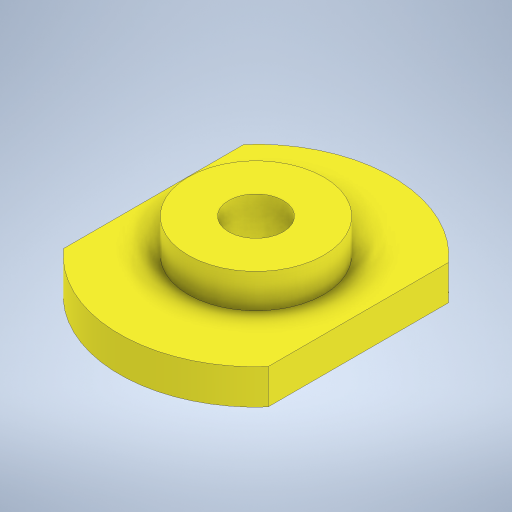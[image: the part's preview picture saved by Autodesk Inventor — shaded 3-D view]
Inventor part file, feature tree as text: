
AUTODESK INVENTOR PART (.ipt)
format: ipt  version: 2024 (Build 280153020, 153B)  size: 266,240 bytes
history: native  units: mm
features: extrude x4, sketch x3, mirror x1, projected_geometry x1
ambient origin geometry x8: Origin, YZ Plane, XZ Plane, XY Plane, X Axis, Y Axis, Z Axis, Center Point
bodies: Solid1 (feature_tree)
feature tree (9):
  sketch  "Sketch1"  dims[d0=7.95mm d1=3.2mm]
  extrude  "Extrusion1"  Depth=3.2mm
  extrude  "Extrusion2"  Depth=2.0mm TaperAngle=0.0deg
  extrude  "Extrusion4"  Depth=2.0mm
  mirror  "Mirror1"
  extrude  "Extrusion5"  Depth=2.0mm TaperAngle=0.0deg
  sketch  "Sketch3"  dims[d2=16.0mm d3=2.0mm d4=0.0mm]
  sketch  "Sketch4"  dims[d5=3.8mm d6=0.0mm d11=2.0mm d13=6.75mm d14=0.0mm d15=1.75mm d16=0.0mm]
  projected_geometry  "Projected Loop1"
